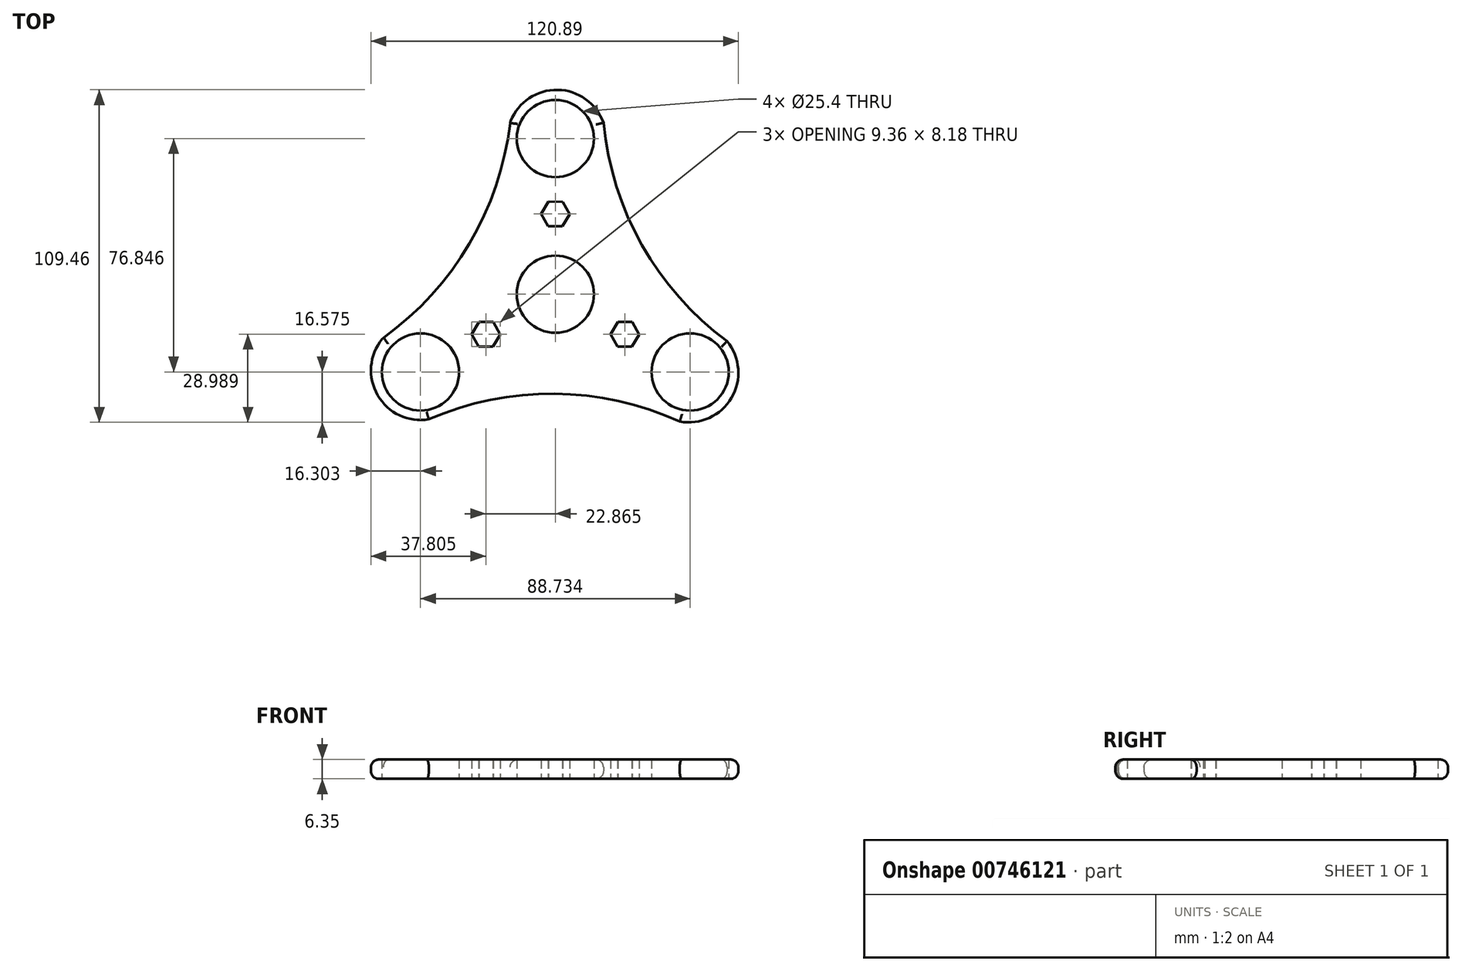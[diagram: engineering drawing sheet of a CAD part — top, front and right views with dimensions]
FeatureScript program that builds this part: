
annotation { "Feature Type Name" : "Feature", "Feature Type Description" : "" }
export const myFeature = defineFeature(function(context is Context, id is Id, definition is map)
    precondition{}
    {
        {
            var Q0;
            Q0=qCreatedBy(makeId("Top.planeOp"),FACE);
            var sketch = newSketch(context, id + "F0", { "sketchPlane" : qUnion([Q0])});
            skCircle(sketch, "E0", {"center": v(0, 0) * mm, "radius": 12.7 * mm});
            skCircle(sketch, "E1", {"center": v(0, 51.23) * mm, "radius": 12.7 * mm});
            skCircle(sketch, "E2.1.0", {"center": v(-44.37, -25.62) * mm, "radius": 12.7 * mm});
            skCircle(sketch, "E2.2.0", {"center": v(44.37, -25.62) * mm, "radius": 12.7 * mm});
            skArc(sketch, "E3", {"start": v(15.84, 56.4) * mm, "mid": v(0.59, 67.27) * mm, "end": v(-14.84, 56.66) * mm});
            skArc(sketch, "E4.1.0", {"start": v(-56.77, -14.49) * mm, "mid": v(-58.55, -33.13) * mm, "end": v(-41.65, -41.18) * mm});
            skArc(sketch, "E4.2.0", {"start": v(40.93, -41.92) * mm, "mid": v(57.96, -34.14) * mm, "end": v(56.49, -15.47) * mm});
            skArc(sketch, "E5", {"start": v(-56.77, -14.49) * mm, "mid": v(-28.26, 16.64) * mm, "end": v(-14.84, 56.66) * mm});
            skArc(sketch, "E6.1.0", {"start": v(40.93, -41.92) * mm, "mid": v(-0.28, -32.8) * mm, "end": v(-41.65, -41.18) * mm});
            skArc(sketch, "E6.2.0", {"start": v(15.84, 56.4) * mm, "mid": v(28.54, 16.15) * mm, "end": v(56.49, -15.47) * mm});
            skCircle(sketch, "E7.cCircle", {"center": v(0, 26.4) * mm, "radius": 4.05 * mm, "construction": true});
            skLineSegment(sketch, "E7.0", {"start": v(4.68, 26.33) * mm, "end": v(2.28, 22.31) * mm});
            skLineSegment(sketch, "E7.1", {"start": v(2.28, 22.31) * mm, "end": v(-2.4, 22.39) * mm});
            skLineSegment(sketch, "E7.2", {"start": v(-2.4, 22.39) * mm, "end": v(-4.68, 26.48) * mm});
            skLineSegment(sketch, "E7.3", {"start": v(-4.68, 26.48) * mm, "end": v(-2.28, 30.5) * mm});
            skLineSegment(sketch, "E7.4", {"start": v(-2.28, 30.5) * mm, "end": v(2.4, 30.42) * mm});
            skLineSegment(sketch, "E7.5", {"start": v(2.4, 30.42) * mm, "end": v(4.68, 26.33) * mm});
            skPoint(sketch, "E7.0.midPoint", {"position": v(3.48, 24.32) * mm});
            skLineSegment(sketch, "E8.1.0", {"start": v(-27.54, -13.13) * mm, "end": v(-25.14, -9.11) * mm});
            skLineSegment(sketch, "E8.1.1", {"start": v(-25.14, -9.11) * mm, "end": v(-20.46, -9.19) * mm});
            skLineSegment(sketch, "E8.1.2", {"start": v(-20.46, -9.19) * mm, "end": v(-18.19, -13.27) * mm});
            skLineSegment(sketch, "E8.1.3", {"start": v(-18.19, -13.27) * mm, "end": v(-20.6, -17.29) * mm});
            skLineSegment(sketch, "E8.1.4", {"start": v(-20.6, -17.29) * mm, "end": v(-25.27, -17.22) * mm});
            skLineSegment(sketch, "E8.1.5", {"start": v(-25.27, -17.22) * mm, "end": v(-27.54, -13.13) * mm});
            skLineSegment(sketch, "E8.2.0", {"start": v(25.14, -17.29) * mm, "end": v(20.46, -17.22) * mm});
            skLineSegment(sketch, "E8.2.1", {"start": v(20.46, -17.22) * mm, "end": v(18.19, -13.13) * mm});
            skLineSegment(sketch, "E8.2.2", {"start": v(18.19, -13.13) * mm, "end": v(20.6, -9.11) * mm});
            skLineSegment(sketch, "E8.2.3", {"start": v(20.6, -9.11) * mm, "end": v(25.27, -9.19) * mm});
            skLineSegment(sketch, "E8.2.4", {"start": v(25.27, -9.19) * mm, "end": v(27.54, -13.27) * mm});
            skLineSegment(sketch, "E8.2.5", {"start": v(27.54, -13.27) * mm, "end": v(25.14, -17.29) * mm});
            skSolve(sketch);
        }
        {
            var Q0;
            Q0=makeQuery(id+"F0.imprint","IMPRINT",FACE,{"disambiguationData":[TD([[makeQuery(id+"F0.imprint","IMPRINT",EDGE,{"derivedFrom":sQuery(id+"F0.wireOp",EDGE,"E0")}),-1.0]])]});
            extrude(context, id + "F1", {"entities" : qUnion([Q0]), "depth" : 6.35 * mm, "offsetDistance" : 25.4 * mm});
        }
        {
            var Q0;
            Q0=makeQuery(id+"F1.opExtrude","CAP_EDGE",EDGE,{"disambiguationData":[OSD([sQuery(id+"F0.wireOp",EDGE,"E5")])],"isStart":false});
            fillet(context, id + "F2", {"entities" : qUnion([Q0]), "radius" : 2.54 * mm, "tangentPropagation" : true, "allowEdgeOverflow" : false});
        }
        {
            var Q0;
            Q0=makeQuery(id+"F1.opExtrude","CAP_EDGE",EDGE,{"disambiguationData":[OSD([sQuery(id+"F0.wireOp",EDGE,"E3")])],"isStart":false});
            var Q1;
            Q1=makeQuery(id+"F1.opExtrude","CAP_EDGE",EDGE,{"disambiguationData":[OSD([sQuery(id+"F0.wireOp",EDGE,"E6.2.0")])],"isStart":false});
            var Q2;
            Q2=makeQuery(id+"F1.opExtrude","CAP_EDGE",EDGE,{"disambiguationData":[OSD([sQuery(id+"F0.wireOp",EDGE,"E4.2.0")])],"isStart":false});
            var Q3;
            Q3=makeQuery(id+"F1.opExtrude","CAP_EDGE",EDGE,{"disambiguationData":[OSD([sQuery(id+"F0.wireOp",EDGE,"E6.1.0")])],"isStart":false});
            var Q4;
            Q4=makeQuery(id+"F1.opExtrude","CAP_EDGE",EDGE,{"disambiguationData":[OSD([sQuery(id+"F0.wireOp",EDGE,"E4.1.0")])],"isStart":false});
            fillet(context, id + "F3", {"entities" : qUnion([Q0, Q1, Q2, Q3, Q4]), "radius" : 2.54 * mm, "tangentPropagation" : true, "allowEdgeOverflow" : false});
        }
        {
            var Q0;
            Q0=makeQuery(id+"F1.opExtrude","CAP_EDGE",EDGE,{"disambiguationData":[OSD([sQuery(id+"F0.wireOp",EDGE,"E5")])],"isStart":true});
            var Q1;
            Q1=makeQuery(id+"F1.opExtrude","CAP_EDGE",EDGE,{"disambiguationData":[OSD([sQuery(id+"F0.wireOp",EDGE,"E4.1.0")])],"isStart":true});
            var Q2;
            Q2=makeQuery(id+"F1.opExtrude","CAP_EDGE",EDGE,{"disambiguationData":[OSD([sQuery(id+"F0.wireOp",EDGE,"E6.1.0")])],"isStart":true});
            var Q3;
            Q3=makeQuery(id+"F1.opExtrude","CAP_EDGE",EDGE,{"disambiguationData":[OSD([sQuery(id+"F0.wireOp",EDGE,"E4.2.0")])],"isStart":true});
            var Q4;
            Q4=makeQuery(id+"F1.opExtrude","CAP_EDGE",EDGE,{"disambiguationData":[OSD([sQuery(id+"F0.wireOp",EDGE,"E6.2.0")])],"isStart":true});
            var Q5;
            Q5=makeQuery(id+"F1.opExtrude","CAP_EDGE",EDGE,{"disambiguationData":[OSD([sQuery(id+"F0.wireOp",EDGE,"E3")])],"isStart":true});
            fillet(context, id + "F4", {"entities" : qUnion([Q0, Q1, Q2, Q3, Q4, Q5]), "radius" : 2.54 * mm, "tangentPropagation" : true, "allowEdgeOverflow" : false});
        }
    });
